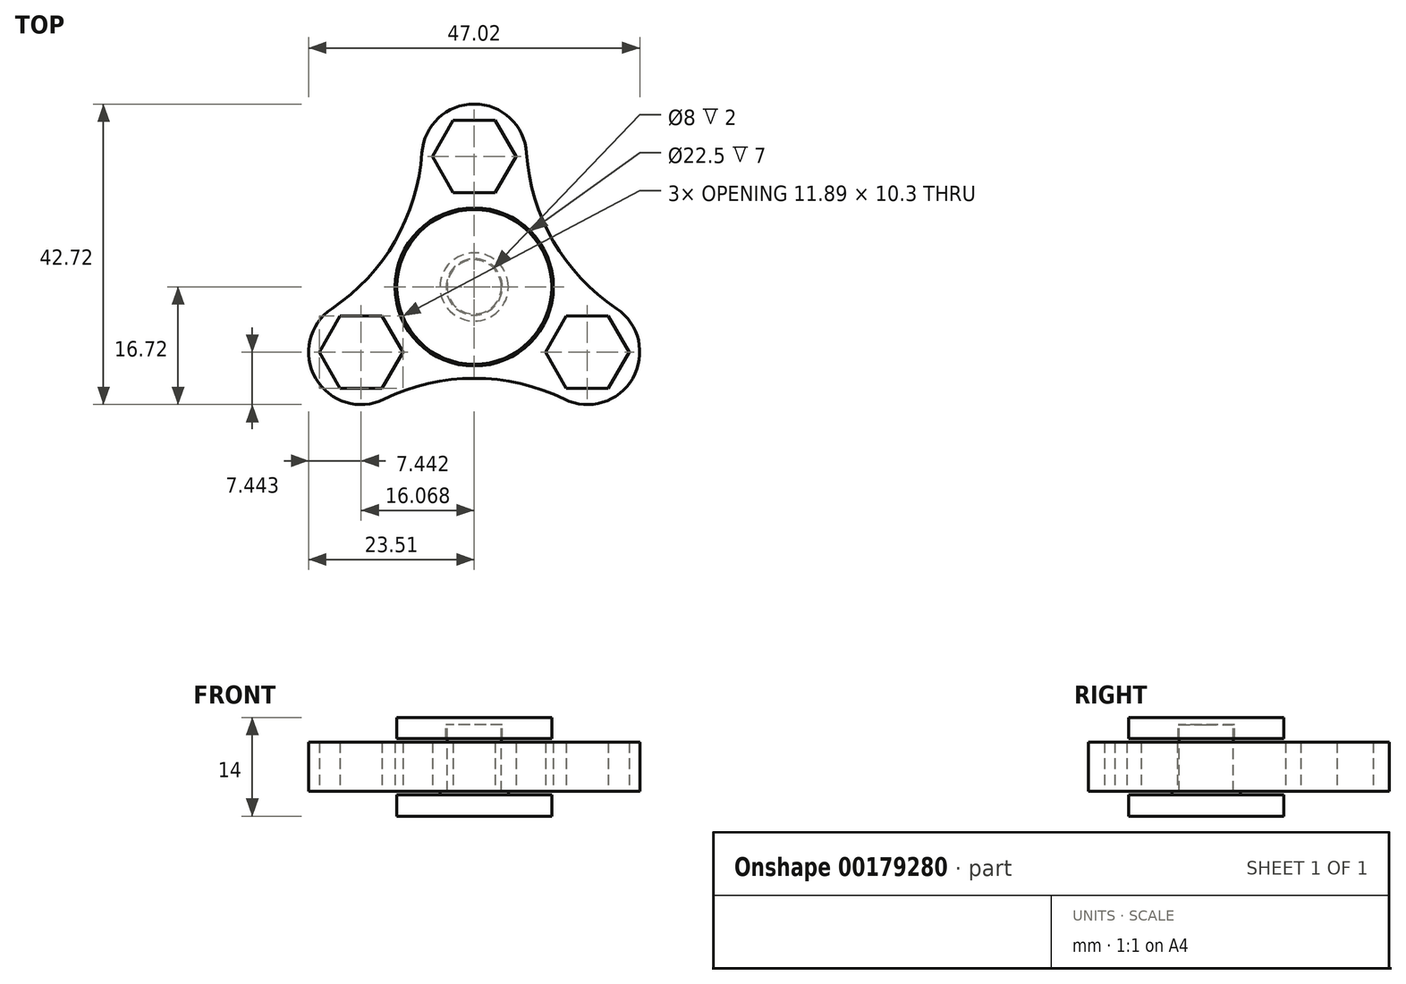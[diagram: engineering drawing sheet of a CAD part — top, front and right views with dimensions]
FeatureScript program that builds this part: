
annotation { "Feature Type Name" : "Feature", "Feature Type Description" : "" }
export const myFeature = defineFeature(function(context is Context, id is Id, definition is map)
    precondition{}
    {
        {
            var Q0;
            Q0=qCreatedBy(makeId("Top.planeOp"),FACE);
            var sketch = newSketch(context, id + "F0", { "sketchPlane" : qUnion([Q0])});
            skCircle(sketch, "E0", {"center": v(0, 0) * mm, "radius": 26 * mm, "construction": true});
            skCircle(sketch, "E1.cCircle", {"center": v(0, 18.55) * mm, "radius": 5.95 * mm, "construction": true});
            skLineSegment(sketch, "E1.0", {"start": v(5.95, 18.55) * mm, "end": v(2.97, 13.4) * mm});
            skLineSegment(sketch, "E1.1", {"start": v(2.97, 13.4) * mm, "end": v(-2.97, 13.4) * mm});
            skLineSegment(sketch, "E1.2", {"start": v(-2.97, 13.4) * mm, "end": v(-5.95, 18.55) * mm});
            skLineSegment(sketch, "E1.3", {"start": v(-5.95, 18.55) * mm, "end": v(-2.97, 23.7) * mm});
            skLineSegment(sketch, "E1.4", {"start": v(-2.97, 23.7) * mm, "end": v(2.97, 23.7) * mm});
            skLineSegment(sketch, "E1.5", {"start": v(2.97, 23.7) * mm, "end": v(5.95, 18.55) * mm});
            skArc(sketch, "E2", {"start": v(7.43, 19.05) * mm, "mid": v(0, 26) * mm, "end": v(-7.43, 19.05) * mm});
            skArc(sketch, "E3.1.0", {"start": v(-20.21, -3.1) * mm, "mid": v(-22.52, -13) * mm, "end": v(-12.78, -15.96) * mm});
            skLineSegment(sketch, "E3.1.1", {"start": v(-19.04, -14.43) * mm, "end": v(-22.01, -9.28) * mm});
            skLineSegment(sketch, "E3.1.2", {"start": v(-13.1, -14.43) * mm, "end": v(-19.04, -14.43) * mm});
            skLineSegment(sketch, "E3.1.3", {"start": v(-10.12, -9.28) * mm, "end": v(-13.1, -14.43) * mm});
            skLineSegment(sketch, "E3.1.4", {"start": v(-13.1, -4.13) * mm, "end": v(-10.12, -9.28) * mm});
            skLineSegment(sketch, "E3.1.5", {"start": v(-19.04, -4.13) * mm, "end": v(-13.1, -4.13) * mm});
            skLineSegment(sketch, "E3.1.6", {"start": v(-22.01, -9.28) * mm, "end": v(-19.04, -4.13) * mm});
            skArc(sketch, "E3.2.0", {"start": v(12.78, -15.96) * mm, "mid": v(22.52, -13) * mm, "end": v(20.21, -3.1) * mm});
            skLineSegment(sketch, "E3.2.1", {"start": v(22.01, -9.28) * mm, "end": v(19.04, -14.43) * mm});
            skLineSegment(sketch, "E3.2.2", {"start": v(19.04, -4.13) * mm, "end": v(22.01, -9.28) * mm});
            skLineSegment(sketch, "E3.2.3", {"start": v(13.1, -4.13) * mm, "end": v(19.04, -4.13) * mm});
            skLineSegment(sketch, "E3.2.4", {"start": v(10.12, -9.28) * mm, "end": v(13.1, -4.13) * mm});
            skLineSegment(sketch, "E3.2.5", {"start": v(13.1, -14.43) * mm, "end": v(10.12, -9.28) * mm});
            skLineSegment(sketch, "E3.2.6", {"start": v(19.04, -14.43) * mm, "end": v(13.1, -14.43) * mm});
            skArc(sketch, "E4", {"start": v(7.43, 19.05) * mm, "mid": v(11.25, 6.5) * mm, "end": v(20.21, -3.1) * mm});
            skArc(sketch, "E5.1.0", {"start": v(-20.21, -3.1) * mm, "mid": v(-11.25, 6.5) * mm, "end": v(-7.43, 19.05) * mm});
            skArc(sketch, "E5.2.0", {"start": v(12.78, -15.96) * mm, "mid": v(0, -13) * mm, "end": v(-12.78, -15.96) * mm});
            skPoint(sketch, "E6.endSnap0", {"position": v(0, -13) * mm});
            skCircle(sketch, "E7", {"center": v(0, 0) * mm, "radius": 11.25 * mm});
            skSolve(sketch);
        }
        {
            var Q0;
            Q0 = qSketchRegion(id + "F0", true);
            extrude(context, id + "F1", {"entities" : qUnion([Q0]), "depth" : 7 * mm, "offsetDistance" : 25 * mm});
        }
        {
            var Q0;
            Q0=qCreatedBy(makeId("Right.planeOp"),FACE);
            var sketch = newSketch(context, id + "F2", { "sketchPlane" : qUnion([Q0])});
            skLineSegment(sketch, "E8.bottom", {"start": v(-3.85, 7) * mm, "end": v(-3.95, 7) * mm});
            skLineSegment(sketch, "E8.top", {"start": v(-3.85, 0) * mm, "end": v(-3.95, 0) * mm});
            skLineSegment(sketch, "E8.left", {"start": v(-3.85, 7) * mm, "end": v(-3.85, 0) * mm});
            skLineSegment(sketch, "E8.right", {"start": v(-3.95, 7) * mm, "end": v(-3.95, 0) * mm});
            skLineSegment(sketch, "E9", {"start": v(0, 14.83) * mm, "end": v(0, -7.53) * mm, "construction": true});
            skLineSegment(sketch, "E10", {"start": v(0, 9.5) * mm, "end": v(-3.85, 9.5) * mm});
            skLineSegment(sketch, "E11", {"start": v(-3.85, 9.5) * mm, "end": v(-3.85, 0) * mm});
            skLineSegment(sketch, "E12", {"start": v(-3.85, 0) * mm, "end": v(-4.85, 0) * mm});
            skLineSegment(sketch, "E13", {"start": v(-4.85, 0) * mm, "end": v(-4.85, -0.5) * mm});
            skLineSegment(sketch, "E14", {"start": v(-4.85, -0.5) * mm, "end": v(-11, -0.5) * mm});
            skLineSegment(sketch, "E15", {"start": v(-11, -0.5) * mm, "end": v(-11, -3.5) * mm});
            skLineSegment(sketch, "E16", {"start": v(-11, -3.5) * mm, "end": v(0, -3.5) * mm});
            skLineSegment(sketch, "E17", {"start": v(0, -3.5) * mm, "end": v(0, 9.5) * mm});
            skLineSegment(sketch, "E18", {"start": v(0, 10.5) * mm, "end": v(-11, 10.5) * mm});
            skLineSegment(sketch, "E19", {"start": v(-11, 10.5) * mm, "end": v(-11, 7.5) * mm});
            skLineSegment(sketch, "E20", {"start": v(-4, 7.5) * mm, "end": v(-11, 7.5) * mm});
            skLineSegment(sketch, "E21", {"start": v(-3.85, 7.5) * mm, "end": v(-3.85, 9.5) * mm});
            skLineSegment(sketch, "E22", {"start": v(-3.85, 9.5) * mm, "end": v(0, 9.5) * mm});
            skLineSegment(sketch, "E23", {"start": v(0, 9.5) * mm, "end": v(0, 10.5) * mm});
            skLineSegment(sketch, "E24", {"start": v(-3.85, 9.5) * mm, "end": v(-4, 9.5) * mm});
            skLineSegment(sketch, "E25", {"start": v(-4, 9.5) * mm, "end": v(-4, 7.5) * mm});
            skSolve(sketch);
        }
        {
            var Q0;
            {var subQ0=sQuery(id+"F2.wireOp",EDGE,"E12");Q0=makeQuery(id+"F2.imprint","IMPRINT",FACE,{"disambiguationData":[TD([[makeQuery(id+"F2.imprint","IMPRINT",EDGE,{"derivedFrom":subQ0}),1.0]])]});}
            var Q1;
            Q1=sQuery(id+"F2.wireOp",EDGE,"E9");
            revolve(context, id + "F3", {"surfaceOperationType" : NewSurfaceOperationType.NEW, "entities" : qUnion([Q0]), "axis" : qUnion([Q1]), "revolveType" : RevolveType.FULL});
        }
        {
            var Q0;
            Q0=makeQuery(id+"F2.imprint","IMPRINT",FACE,{"disambiguationData":[TD([[makeQuery(id+"F2.imprint","IMPRINT",EDGE,{"derivedFrom":sQuery(id+"F2.wireOp",EDGE,"E18")}),1.0]])]});
            var Q1;
            Q1=sQuery(id+"F2.wireOp",EDGE,"E9");
            revolve(context, id + "F4", {"surfaceOperationType" : NewSurfaceOperationType.NEW, "entities" : qUnion([Q0]), "axis" : qUnion([Q1]), "revolveType" : RevolveType.FULL});
        }
    });
